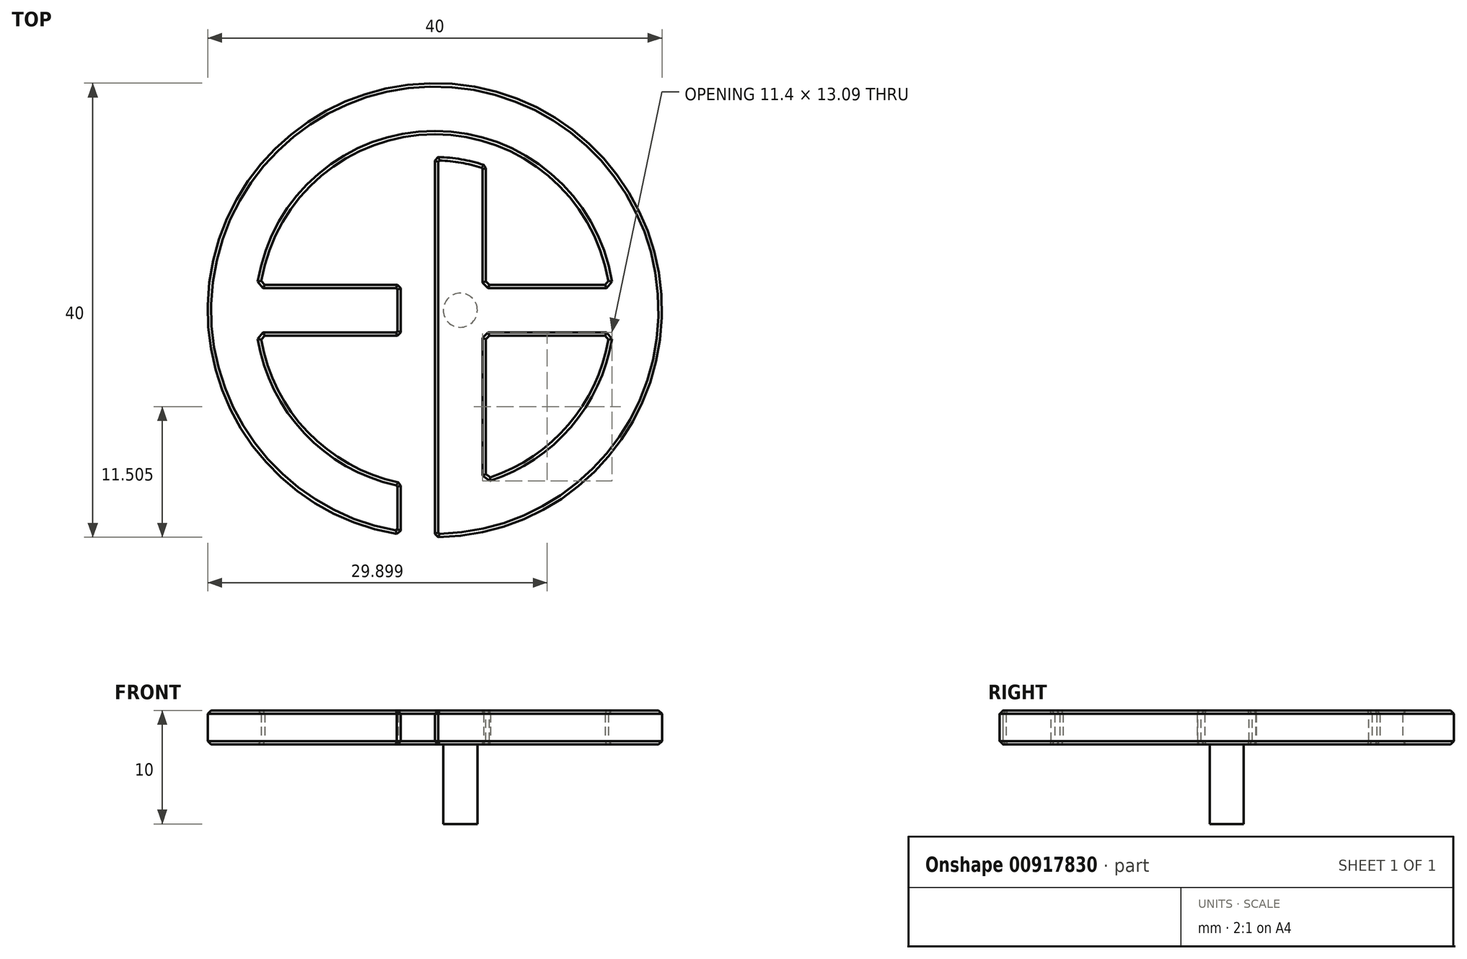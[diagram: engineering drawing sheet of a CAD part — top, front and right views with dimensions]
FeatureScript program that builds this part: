
annotation { "Feature Type Name" : "Feature", "Feature Type Description" : "" }
export const myFeature = defineFeature(function(context is Context, id is Id, definition is map)
    precondition{}
    {
        {
            var Q0;
            Q0=qCreatedBy(makeId("Top.planeOp"),FACE);
            var sketch = newSketch(context, id + "F0", { "sketchPlane" : qUnion([Q0])});
            skCircle(sketch, "E0", {"center": v(0, 0) * mm, "radius": 20 * mm});
            skCircle(sketch, "E1", {"center": v(0, 0) * mm, "radius": 15.5 * mm});
            skLineSegment(sketch, "E2", {"start": v(0, 15.5) * mm, "end": v(0, 20) * mm, "construction": true});
            skLineSegment(sketch, "E3", {"start": v(0, -15.5) * mm, "end": v(0, -20) * mm});
            skLineSegment(sketch, "E4", {"start": v(0, 0) * mm, "end": v(-15.5, 0) * mm, "construction": true});
            skLineSegment(sketch, "E5", {"start": v(-15.5, 0) * mm, "end": v(-20, 0) * mm, "construction": true});
            skLineSegment(sketch, "E6", {"start": v(0, 0) * mm, "end": v(15.5, 0) * mm, "construction": true});
            skLineSegment(sketch, "E7", {"start": v(15.5, 0) * mm, "end": v(20, 0) * mm, "construction": true});
            skLineSegment(sketch, "E8", {"start": v(-3, -15.2) * mm, "end": v(-3, -19.77) * mm});
            skLineSegment(sketch, "E9", {"start": v(-15.34, 2.25) * mm, "end": v(15.34, 2.25) * mm});
            skLineSegment(sketch, "E10", {"start": v(15.34, -2.25) * mm, "end": v(-15.34, -2.25) * mm});
            skLineSegment(sketch, "E11", {"start": v(-3, -2.25) * mm, "end": v(-3, 2.25) * mm});
            skCircle(sketch, "E12", {"center": v(0, 0) * mm, "radius": 13.5 * mm});
            skLineSegment(sketch, "E13", {"start": v(4.5, -14.83) * mm, "end": v(4.5, 12.73) * mm});
            skLineSegment(sketch, "E14", {"start": v(0, 0) * mm, "end": v(0, 13.5) * mm});
            skLineSegment(sketch, "E15", {"start": v(0, 13.5) * mm, "end": v(0, 15.5) * mm, "construction": true});
            skLineSegment(sketch, "E16", {"start": v(0, 0) * mm, "end": v(0, -13.5) * mm});
            skLineSegment(sketch, "E17", {"start": v(0, -13.5) * mm, "end": v(0, -15.5) * mm});
            skSolve(sketch);
        }
        {
            var Q0;
            {var subQ7=sQuery(id+"F0.wireOp",EDGE,"E3");Q0=makeQuery(id+"F0.imprint","IMPRINT",FACE,{"disambiguationData":[TD([[makeQuery(id+"F0.imprint","IMPRINT",EDGE,{"derivedFrom":subQ7}),1.0]])]});}
            var Q1;
            {var subQ0=sQuery(id+"F0.wireOp",EDGE,"E9");var subQ1=sQuery(id+"F0.wireOp",EDGE,"E1");var subQ2=makeQuery(id+"F0.imprint","INTERSECT",VERTEX,{"disambiguationData":[OD(0.0)],"derivedFrom":[subQ1,subQ0]});Q1=makeQuery(id+"F0.imprint","IMPRINT",FACE,{"disambiguationData":[TD([[makeQuery(id+"F0.imprint","IMPRINT",EDGE,{"disambiguationData":[TD([[subQ2,-1.0]])],"derivedFrom":subQ1}),1.0]])]});}
            var Q2;
            {var subQ0=sQuery(id+"F0.wireOp",EDGE,"E11");Q2=makeQuery(id+"F0.imprint","IMPRINT",FACE,{"disambiguationData":[TD([[makeQuery(id+"F0.imprint","IMPRINT",EDGE,{"derivedFrom":subQ0}),1.0]])]});}
            var Q3;
            {var subQ0=sQuery(id+"F0.wireOp",EDGE,"E14");var subQ1=sQuery(id+"F0.wireOp",EDGE,"E9");var subQ2=makeQuery(id+"F0.imprint","INTERSECT",VERTEX,{"derivedFrom":[subQ1,subQ0]});Q3=makeQuery(id+"F0.imprint","IMPRINT",FACE,{"disambiguationData":[TD([[makeQuery(id+"F0.imprint","IMPRINT",EDGE,{"disambiguationData":[TD([[subQ2,-1.0]])],"derivedFrom":subQ1}),1.0]])]});}
            var Q4;
            {var subQ1=sQuery(id+"F0.wireOp",EDGE,"E14");var subQ3=sQuery(id+"F0.wireOp",EDGE,"E9");var subQ4=makeQuery(id+"F0.imprint","INTERSECT",VERTEX,{"derivedFrom":[subQ3,subQ1]});Q4=makeQuery(id+"F0.imprint","IMPRINT",FACE,{"disambiguationData":[TD([[makeQuery(id+"F0.imprint","IMPRINT",EDGE,{"disambiguationData":[TD([[subQ4,-1.0]])],"derivedFrom":subQ3}),-1.0]])]});}
            var Q5;
            {var subQ0=sQuery(id+"F0.wireOp",EDGE,"E13");var subQ1=sQuery(id+"F0.wireOp",EDGE,"E10");var subQ2=makeQuery(id+"F0.imprint","INTERSECT",VERTEX,{"derivedFrom":[subQ1,subQ0]});Q5=makeQuery(id+"F0.imprint","IMPRINT",FACE,{"disambiguationData":[TD([[makeQuery(id+"F0.imprint","IMPRINT",EDGE,{"disambiguationData":[TD([[subQ2,-1.0]])],"derivedFrom":subQ1}),1.0]])]});}
            var Q6;
            {var subQ0=sQuery(id+"F0.wireOp",EDGE,"E17");Q6=makeQuery(id+"F0.imprint","IMPRINT",FACE,{"disambiguationData":[TD([[makeQuery(id+"F0.imprint","IMPRINT",EDGE,{"derivedFrom":subQ0}),1.0]])]});}
            var Q7;
            {var subQ0=sQuery(id+"F0.wireOp",EDGE,"E13");var subQ1=sQuery(id+"F0.wireOp",EDGE,"E9");var subQ2=makeQuery(id+"F0.imprint","INTERSECT",VERTEX,{"derivedFrom":[subQ1,subQ0]});Q7=makeQuery(id+"F0.imprint","IMPRINT",FACE,{"disambiguationData":[TD([[makeQuery(id+"F0.imprint","IMPRINT",EDGE,{"disambiguationData":[TD([[subQ2,-1.0]])],"derivedFrom":subQ1}),-1.0]])]});}
            var Q8;
            {var subQ0=sQuery(id+"F0.wireOp",EDGE,"E9");var subQ1=sQuery(id+"F0.wireOp",EDGE,"E1");var subQ2=makeQuery(id+"F0.imprint","INTERSECT",VERTEX,{"disambiguationData":[OD(1.0)],"derivedFrom":[subQ1,subQ0]});Q8=makeQuery(id+"F0.imprint","IMPRINT",FACE,{"disambiguationData":[TD([[makeQuery(id+"F0.imprint","IMPRINT",EDGE,{"disambiguationData":[TD([[subQ2,1.0]])],"derivedFrom":subQ1}),1.0]])]});}
            extrude(context, id + "F1", {"entities" : qUnion([Q0, Q1, Q2, Q3, Q4, Q5, Q6, Q7, Q8]), "depth" : 3 * mm, "offsetDistance" : 25 * mm});
        }
        {
            var Q0;
            Q0=makeQuery(id+"F1.opExtrude","CAP_FACE",FACE,{"disambiguationData":[OSD([sQuery(id+"F0.wireOp",EDGE,"E0"),sQuery(id+"F0.wireOp",EDGE,"E1"),sQuery(id+"F0.wireOp",EDGE,"E3"),sQuery(id+"F0.wireOp",EDGE,"E8"),sQuery(id+"F0.wireOp",EDGE,"E9"),sQuery(id+"F0.wireOp",EDGE,"E10"),sQuery(id+"F0.wireOp",EDGE,"E11"),sQuery(id+"F0.wireOp",EDGE,"E12"),sQuery(id+"F0.wireOp",EDGE,"E13"),sQuery(id+"F0.wireOp",EDGE,"E14"),sQuery(id+"F0.wireOp",EDGE,"E16"),sQuery(id+"F0.wireOp",EDGE,"E17")])],"isStart":true});
            var sketch = newSketch(context, id + "F2", { "sketchPlane" : qUnion([Q0])});
            skLineSegment(sketch, "E18", {"start": v(4.5, 2.25) * mm, "end": v(0, 2.25) * mm, "construction": true});
            skPoint(sketch, "E19", {"position": v(2.25, 2.25) * mm});
            skCircle(sketch, "E20", {"center": v(2.25, 0) * mm, "radius": 1.5 * mm});
            skSolve(sketch);
        }
        {
            var Q0;
            Q0=makeQuery(id+"F1.opExtrude","SWEPT_EDGE",EDGE,{"disambiguationData":[OSD([sQuery(id+"F0.wireOp",EDGE,"E10"),sQuery(id+"F0.wireOp",EDGE,"E11")])]});
            var Q1;
            Q1=makeQuery(id+"F1.opExtrude","SWEPT_EDGE",EDGE,{"disambiguationData":[OSD([sQuery(id+"F0.wireOp",EDGE,"E9"),sQuery(id+"F0.wireOp",EDGE,"E11")])]});
            var Q2;
            {var subQ0=sQuery(id+"F0.wireOp",EDGE,"E9");var subQ1=sQuery(id+"F0.wireOp",EDGE,"E1");Q2=makeQuery(id+"F1.opExtrude","SWEPT_EDGE",EDGE,{"disambiguationData":[OSD([subQ1,subQ0]),TDD([makeQuery(id+"F0.imprint","INTERSECT",VERTEX,{"disambiguationData":[OD(0.0)],"derivedFrom":[subQ1,subQ0]})])]});}
            var Q3;
            Q3=makeQuery(id+"F1.opExtrude","SWEPT_EDGE",EDGE,{"disambiguationData":[OSD([sQuery(id+"F0.wireOp",EDGE,"E12"),sQuery(id+"F0.wireOp",EDGE,"E14")])]});
            var Q4;
            Q4=makeQuery(id+"F1.opExtrude","SWEPT_EDGE",EDGE,{"disambiguationData":[OSD([sQuery(id+"F0.wireOp",EDGE,"E12"),sQuery(id+"F0.wireOp",EDGE,"E13")])]});
            var Q5;
            Q5=makeQuery(id+"F1.opExtrude","SWEPT_EDGE",EDGE,{"disambiguationData":[OSD([sQuery(id+"F0.wireOp",EDGE,"E9"),sQuery(id+"F0.wireOp",EDGE,"E13")])]});
            var Q6;
            {var subQ0=sQuery(id+"F0.wireOp",EDGE,"E9");var subQ1=sQuery(id+"F0.wireOp",EDGE,"E1");Q6=makeQuery(id+"F1.opExtrude","SWEPT_EDGE",EDGE,{"disambiguationData":[OSD([subQ1,subQ0]),TDD([makeQuery(id+"F0.imprint","INTERSECT",VERTEX,{"disambiguationData":[OD(1.0)],"derivedFrom":[subQ1,subQ0]})])]});}
            var Q7;
            {var subQ0=sQuery(id+"F0.wireOp",EDGE,"E10");var subQ1=sQuery(id+"F0.wireOp",EDGE,"E1");Q7=makeQuery(id+"F1.opExtrude","SWEPT_EDGE",EDGE,{"disambiguationData":[OSD([subQ1,subQ0]),TDD([makeQuery(id+"F0.imprint","INTERSECT",VERTEX,{"disambiguationData":[OD(0.0)],"derivedFrom":[subQ1,subQ0]})])]});}
            var Q8;
            Q8=makeQuery(id+"F1.opExtrude","SWEPT_EDGE",EDGE,{"disambiguationData":[OSD([sQuery(id+"F0.wireOp",EDGE,"E10"),sQuery(id+"F0.wireOp",EDGE,"E13")])]});
            var Q9;
            Q9=makeQuery(id+"F1.opExtrude","SWEPT_EDGE",EDGE,{"disambiguationData":[OSD([sQuery(id+"F0.wireOp",EDGE,"E1"),sQuery(id+"F0.wireOp",EDGE,"E13")])]});
            var Q10;
            Q10=makeQuery(id+"F1.opExtrude","SWEPT_EDGE",EDGE,{"disambiguationData":[OSD([sQuery(id+"F0.wireOp",EDGE,"E0"),sQuery(id+"F0.wireOp",EDGE,"E3")])]});
            var Q11;
            Q11=makeQuery(id+"F1.opExtrude","SWEPT_EDGE",EDGE,{"disambiguationData":[OSD([sQuery(id+"F0.wireOp",EDGE,"E0"),sQuery(id+"F0.wireOp",EDGE,"E8")])]});
            var Q12;
            Q12=makeQuery(id+"F1.opExtrude","SWEPT_EDGE",EDGE,{"disambiguationData":[OSD([sQuery(id+"F0.wireOp",EDGE,"E1"),sQuery(id+"F0.wireOp",EDGE,"E8")])]});
            var Q13;
            {var subQ0=sQuery(id+"F0.wireOp",EDGE,"E10");var subQ1=sQuery(id+"F0.wireOp",EDGE,"E1");Q13=makeQuery(id+"F1.opExtrude","SWEPT_EDGE",EDGE,{"disambiguationData":[OSD([subQ1,subQ0]),TDD([makeQuery(id+"F0.imprint","INTERSECT",VERTEX,{"disambiguationData":[OD(1.0)],"derivedFrom":[subQ1,subQ0]})])]});}
            chamfer(context, id + "F3", {"entities" : qUnion([Q0, Q1, Q2, Q3, Q4, Q5, Q6, Q7, Q8, Q9, Q10, Q11, Q12, Q13]), "width" : 0.3 * mm, "tangentPropagation" : true});
        }
        {
            var Q0;
            Q0=makeQuery(id+"F1.opExtrude","CAP_FACE",FACE,{"disambiguationData":[OSD([sQuery(id+"F0.wireOp",EDGE,"E0"),sQuery(id+"F0.wireOp",EDGE,"E1"),sQuery(id+"F0.wireOp",EDGE,"E3"),sQuery(id+"F0.wireOp",EDGE,"E8"),sQuery(id+"F0.wireOp",EDGE,"E9"),sQuery(id+"F0.wireOp",EDGE,"E10"),sQuery(id+"F0.wireOp",EDGE,"E11"),sQuery(id+"F0.wireOp",EDGE,"E12"),sQuery(id+"F0.wireOp",EDGE,"E13"),sQuery(id+"F0.wireOp",EDGE,"E14"),sQuery(id+"F0.wireOp",EDGE,"E16"),sQuery(id+"F0.wireOp",EDGE,"E17")])],"isStart":false});
            var Q1;
            Q1=makeQuery(id+"F1.opExtrude","CAP_FACE",FACE,{"disambiguationData":[OSD([sQuery(id+"F0.wireOp",EDGE,"E0"),sQuery(id+"F0.wireOp",EDGE,"E1"),sQuery(id+"F0.wireOp",EDGE,"E3"),sQuery(id+"F0.wireOp",EDGE,"E8"),sQuery(id+"F0.wireOp",EDGE,"E9"),sQuery(id+"F0.wireOp",EDGE,"E10"),sQuery(id+"F0.wireOp",EDGE,"E11"),sQuery(id+"F0.wireOp",EDGE,"E12"),sQuery(id+"F0.wireOp",EDGE,"E13"),sQuery(id+"F0.wireOp",EDGE,"E14"),sQuery(id+"F0.wireOp",EDGE,"E16"),sQuery(id+"F0.wireOp",EDGE,"E17")])],"isStart":true});
            chamfer(context, id + "F4", {"entities" : qUnion([Q0, Q1]), "width" : 0.3 * mm, "tangentPropagation" : true});
        }
        {
            var Q0;
            Q0=makeQuery(id+"F2.imprint","IMPRINT",FACE,{"disambiguationData":[TD([[makeQuery(id+"F2.imprint","IMPRINT",EDGE,{"derivedFrom":sQuery(id+"F2.wireOp",EDGE,"E20")}),1.0]])]});
            extrude(context, id + "F5", {"entities" : qUnion([Q0]), "operationType" : NewBodyOperationType.ADD, "depth" : 7 * mm, "offsetDistance" : 25 * mm});
        }
    });
